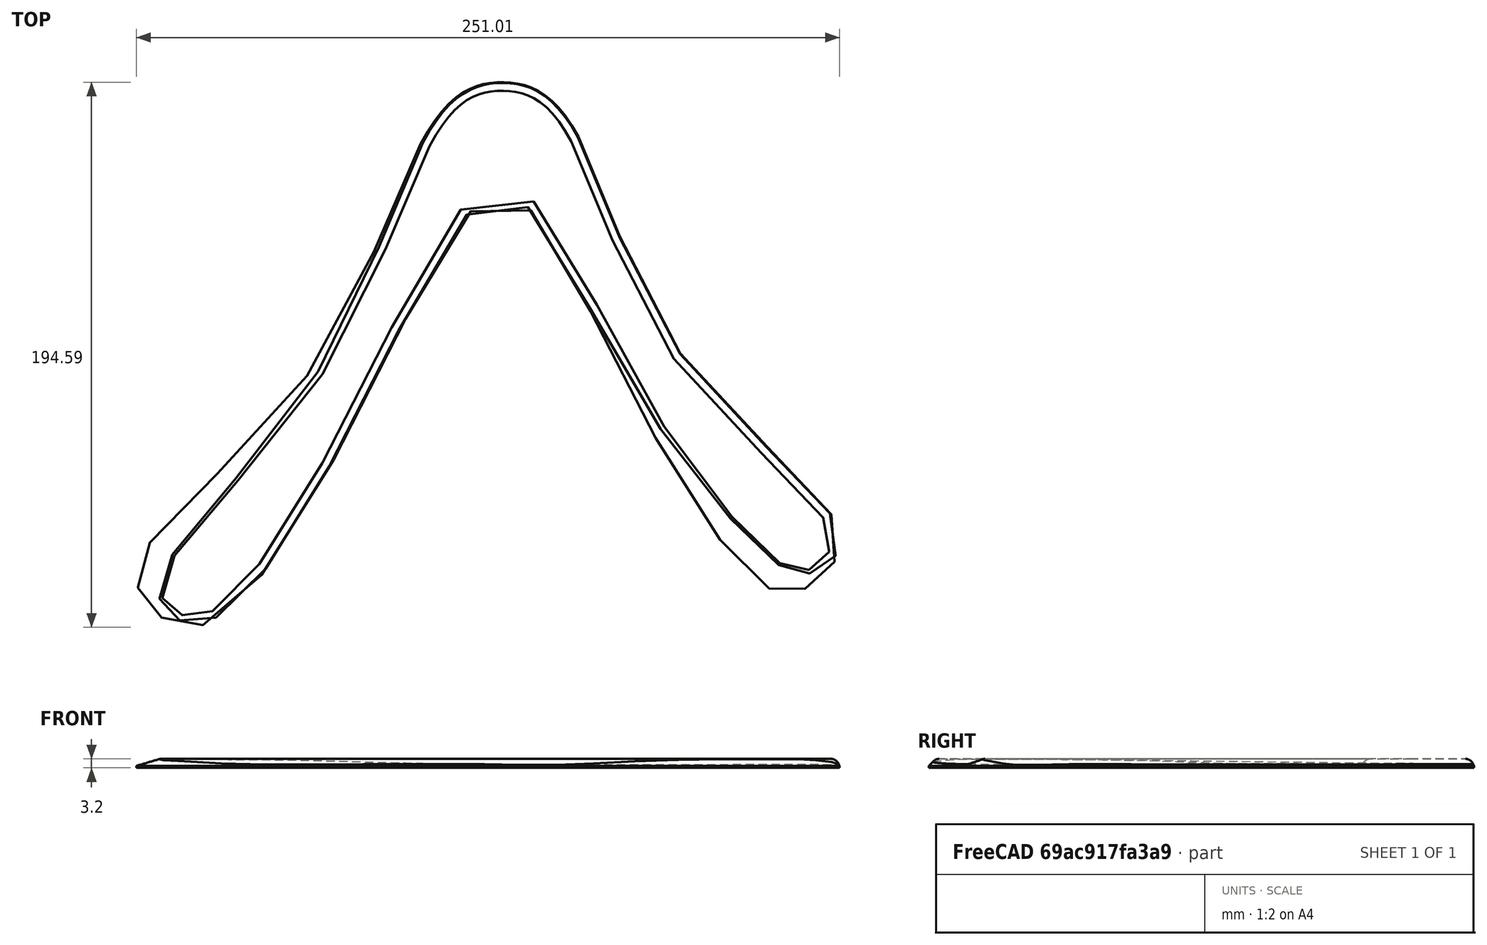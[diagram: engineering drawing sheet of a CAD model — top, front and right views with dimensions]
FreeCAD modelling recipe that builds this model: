
FCSTD DOCUMENT  (FreeCAD 0.19R23756 (Git))
Label: splinebased
License: All rights reserved
LicenseURL: http://en.wikipedia.org/wiki/All_rights_reserved
objects: Sketcher::SketchObject×2, PartDesign::Plane×1, PartDesign::AdditiveLoft×1, PartDesign::Pad×1, PartDesign::Fillet×1, PartDesign::Body×1, Mesh::Feature×1
note: 10 computed .brp shape members not serialized (recipe doc carries the construction recipe); baked Part::Feature solids carry a one-line shape summary decoded from their .brp

FEATURE [Sketcher::SketchObject] Sketch  label="Outline"
  FullyConstrained = false
  MapMode = 5
  Support = -> [XY_Plane]
  sketch-geometry (32):
    g0: LineSegment StartX=0 StartY=0 StartZ=0 EndX=-114.715 EndY=-163.83 EndZ=0
    g1: LineSegment StartX=0 StartY=0 StartZ=0 EndX=103.244 EndY=-147.447 EndZ=0
    g2-g15: Circle x14 (B-spline internal-alignment scaffolding for g16; pole/knot coordinates omitted)
    g16: BSplineCurve PolesCount=14 KnotsCount=15 Degree=3 IsPeriodic=1
    g17-g31: GeomPoint x15 (B-spline internal-alignment scaffolding for g16; pole/knot coordinates omitted)
  constraints (13):
    c: Coincident(g0,g-1)
    c: Coincident(g1,g-1)
    c: Distance(g0) = 200
    c: Distance(g1) = 180
    c: Angle(g0,g1) = 1.22173
    c: Angle(g-2,g0) = 2.53073
    c: PointOnObject(g2,g-2)
    c: Weight(g2) = 1
    c: Equal(g2, g3-g9) x7
    c: PointOnObject(g9,g-2)
    c: Equal(g2, g10-g15) x6
    c: InternalAlignment(g2-g15 -> g16) x14
    c: InternalAlignment(g17-g31 -> g16) x15
FEATURE [PartDesign::Plane] DatumPlane  label="Top Plane"
  AttachmentOffset = pos=(0,0,2.5) rot=(0,0,1;0rad)
  Length = 295.857
  MapMode = 2
  Placement = pos=(0,0,2.5) rot=(0,0,1;0rad)
  ResizeMode = 0
  Support = -> [Sketch]
  Width = 245.15
FEATURE [Sketcher::SketchObject] Sketch001  label="Top Outline"
  FullyConstrained = false
  MapMode = 5
  Placement = pos=(0,0,2.5) rot=(0,0,1;0rad)
  Support = -> [DatumPlane]
  sketch-geometry (30):
    g0-g13: Circle x14 (B-spline internal-alignment scaffolding for g14; pole/knot coordinates omitted)
    g14: BSplineCurve PolesCount=14 KnotsCount=15 Degree=3 IsPeriodic=1
    g15-g29: GeomPoint x15 (B-spline internal-alignment scaffolding for g14; pole/knot coordinates omitted)
  constraints (4):
    c: Weight(g0) = 1
    c: Equal(g0, g1-g13) x13
    c: InternalAlignment(g0-g13 -> g14) x14
    c: InternalAlignment(g15-g29 -> g14) x15
FEATURE [PartDesign::AdditiveLoft] AdditiveLoft  label="Boomerang Loft"
  Closed = true
  Profile = -> Sketch
  Ruled = true
  Sections = -> [Sketch001]
FEATURE [PartDesign::Pad] Pad  label="Bottom Pad"
  BaseFeature = -> AdditiveLoft
  Direction = (1,1,1)
  Length = 0.7
  Length2 = 100
  Profile = -> AdditiveLoft [Face1]
  Type = 0
FEATURE [PartDesign::Fillet] Fillet  label="Airfoil Fillet"
  Base = -> Pad [Face4]
  BaseFeature = -> Pad
  Radius = 3
  SupportTransform = false
FEATURE [PartDesign::Body] Body  label="Boomerang"
  Group = -> [Sketch,DatumPlane,Sketch001,AdditiveLoft,Pad,Fillet]
  Origin = -> Origin
  Tip = -> Fillet
FEATURE [Mesh::Feature] Mesh  label="Boomerang (Meshed)"
